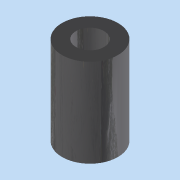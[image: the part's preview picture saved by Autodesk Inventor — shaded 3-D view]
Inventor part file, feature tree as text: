
AUTODESK INVENTOR PART (.ipt)
format: ipt  version: 2015 (Build 190159000, 159)  size: 110,080 bytes
history: native  units: mm
features: extrude x1, sketch x1
ambient origin geometry x8: Origin, YZ Plane, XZ Plane, XY Plane, X Axis, Y Axis, Z Axis, Center Point
bodies: Solid1 (feature_tree)
feature tree (2):
  extrude  "Extrusion1"  Depth=19.0mm
  sketch  "Sketch1"  dims[d0=6.0mm d1=12.0mm d2=19.0mm d3=0.0mm]
